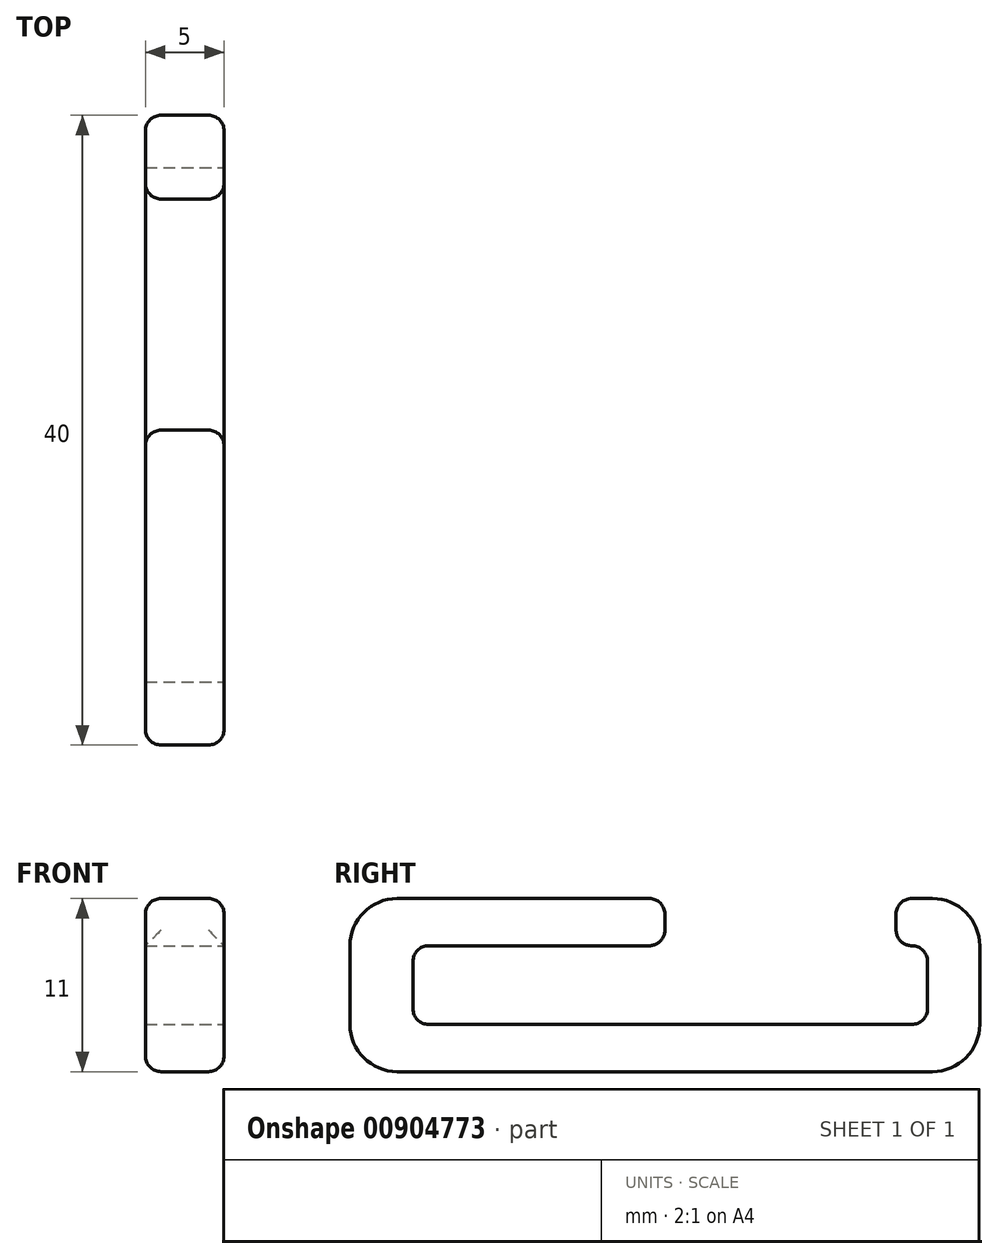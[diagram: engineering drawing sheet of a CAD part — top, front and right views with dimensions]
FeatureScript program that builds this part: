
annotation { "Feature Type Name" : "Feature", "Feature Type Description" : "" }
export const myFeature = defineFeature(function(context is Context, id is Id, definition is map)
    precondition{}
    {
        {
            var Q0;
            Q0=qCreatedBy(makeId("Top.planeOp"),FACE);
            var sketch = newSketch(context, id + "F0", { "sketchPlane" : qUnion([Q0])});
            skCircle(sketch, "E0", {"center": v(0, 0) * mm, "radius": 3 * mm, "construction": true});
            skLineSegment(sketch, "E1", {"start": v(-2.5, 1.66) * mm, "end": v(-2.5, -38.34) * mm});
            skLineSegment(sketch, "E2", {"start": v(-2.5, -38.34) * mm, "end": v(0, -38.34) * mm});
            skLineSegment(sketch, "E3.MirrorCS", {"start": v(2.5, 1.66) * mm, "end": v(2.5, -38.34) * mm});
            skLineSegment(sketch, "E4.MirrorCS", {"start": v(2.5, -38.34) * mm, "end": v(0, -38.34) * mm});
            skLineSegment(sketch, "E5", {"start": v(-2.5, -34.34) * mm, "end": v(2.5, -34.34) * mm});
            skLineSegment(sketch, "E6", {"start": v(-2.5, -18.34) * mm, "end": v(2.5, -18.34) * mm});
            skCircle(sketch, "E7", {"center": v(-5.3, 0) * mm, "radius": 12.5 * mm, "construction": true});
            skLineSegment(sketch, "E8", {"start": v(-2.5, 1.66) * mm, "end": v(2.5, 1.66) * mm});
            skLineSegment(sketch, "E9", {"start": v(-2.5, -1.66) * mm, "end": v(2.5, -1.66) * mm});
            skLineSegment(sketch, "E10", {"start": v(-2.5, -3.66) * mm, "end": v(2.5, -3.66) * mm});
            skSolve(sketch);
        }
        {
            var Q0;
            {var subQ0=sQuery(id+"F0.wireOp",EDGE,"E8");Q0=makeQuery(id+"F0.imprint","IMPRINT",FACE,{"disambiguationData":[TD([[makeQuery(id+"F0.imprint","IMPRINT",EDGE,{"derivedFrom":subQ0}),-1.0]])]});}
            var Q1;
            {var subQ0=sQuery(id+"F0.wireOp",EDGE,"E5");Q1=makeQuery(id+"F0.imprint","IMPRINT",FACE,{"disambiguationData":[TD([[makeQuery(id+"F0.imprint","IMPRINT",EDGE,{"derivedFrom":subQ0}),1.0]])]});}
            var Q2;
            {var subQ0=sQuery(id+"F0.wireOp",EDGE,"E6");Q2=makeQuery(id+"F0.imprint","IMPRINT",FACE,{"disambiguationData":[TD([[makeQuery(id+"F0.imprint","IMPRINT",EDGE,{"derivedFrom":subQ0}),1.0]])]});}
            var Q3;
            {var subQ0=sQuery(id+"F0.wireOp",EDGE,"E9");Q3=makeQuery(id+"F0.imprint","IMPRINT",FACE,{"disambiguationData":[TD([[makeQuery(id+"F0.imprint","IMPRINT",EDGE,{"derivedFrom":subQ0}),-1.0]])]});}
            var Q4;
            {var subQ3=sQuery(id+"F0.wireOp",EDGE,"E2");Q4=makeQuery(id+"F0.imprint","IMPRINT",FACE,{"disambiguationData":[TD([[makeQuery(id+"F0.imprint","IMPRINT",EDGE,{"derivedFrom":subQ3}),1.0]])]});}
            extrude(context, id + "F1", {"entities" : qUnion([Q0, Q1, Q2, Q3, Q4]), "depth" : 3 * mm, "offsetDistance" : 25 * mm});
        }
        {
            var Q0;
            {var subQ0=sQuery(id+"F0.wireOp",EDGE,"E8");Q0=makeQuery(id+"F0.imprint","IMPRINT",FACE,{"disambiguationData":[TD([[makeQuery(id+"F0.imprint","IMPRINT",EDGE,{"derivedFrom":subQ0}),-1.0]])]});}
            var Q1;
            {var subQ0=sQuery(id+"F0.wireOp",EDGE,"E9");Q1=makeQuery(id+"F0.imprint","IMPRINT",FACE,{"disambiguationData":[TD([[makeQuery(id+"F0.imprint","IMPRINT",EDGE,{"derivedFrom":subQ0}),-1.0]])]});}
            var Q2;
            {var subQ3=sQuery(id+"F0.wireOp",EDGE,"E2");Q2=makeQuery(id+"F0.imprint","IMPRINT",FACE,{"disambiguationData":[TD([[makeQuery(id+"F0.imprint","IMPRINT",EDGE,{"derivedFrom":subQ3}),1.0]])]});}
            var Q3;
            {var subQ0=sQuery(id+"F0.wireOp",EDGE,"E5");Q3=makeQuery(id+"F0.imprint","IMPRINT",FACE,{"disambiguationData":[TD([[makeQuery(id+"F0.imprint","IMPRINT",EDGE,{"derivedFrom":subQ0}),1.0]])]});}
            extrude(context, id + "F2", {"entities" : qUnion([Q0, Q1, Q2, Q3]), "operationType" : NewBodyOperationType.ADD, "depth" : 11 * mm, "offsetDistance" : 25 * mm});
        }
        {
            var Q0;
            {var subQ0=sQuery(id+"F0.wireOp",EDGE,"E9");Q0=makeQuery(id+"F0.imprint","IMPRINT",FACE,{"disambiguationData":[TD([[makeQuery(id+"F0.imprint","IMPRINT",EDGE,{"derivedFrom":subQ0}),-1.0]])]});}
            var Q1;
            {var subQ0=sQuery(id+"F0.wireOp",EDGE,"E5");Q1=makeQuery(id+"F0.imprint","IMPRINT",FACE,{"disambiguationData":[TD([[makeQuery(id+"F0.imprint","IMPRINT",EDGE,{"derivedFrom":subQ0}),1.0]])]});}
            extrude(context, id + "F3", {"entities" : qUnion([Q0, Q1]), "operationType" : NewBodyOperationType.REMOVE, "depth" : 8 * mm, "offsetDistance" : 25 * mm, "hasSecondDirection" : true, "secondDirectionOppositeDirection" : false, "secondDirectionDepth" : 3 * mm});
        }
        {
            var Q0;
            Q0=makeQuery(id+"F2.opExtrude","CAP_EDGE",EDGE,{"disambiguationData":[OSD([sQuery(id+"F0.wireOp",EDGE,"E8")])],"isStart":false});
            var Q1;
            Q1=makeQuery(id+"F2.opExtrude","CAP_EDGE",EDGE,{"disambiguationData":[OSD([sQuery(id+"F0.wireOp",EDGE,"E2"),sQuery(id+"F0.wireOp",EDGE,"E4.MirrorCS")])],"isStart":false});
            var Q2;
            Q2=makeQuery(id+"F1.opExtrude","CAP_EDGE",EDGE,{"disambiguationData":[OSD([sQuery(id+"F0.wireOp",EDGE,"E2"),sQuery(id+"F0.wireOp",EDGE,"E4.MirrorCS")])],"isStart":true});
            var Q3;
            Q3=makeQuery(id+"F1.opExtrude","CAP_EDGE",EDGE,{"disambiguationData":[OSD([sQuery(id+"F0.wireOp",EDGE,"E8")])],"isStart":true});
            fillet(context, id + "F4", {"entities" : qUnion([Q0, Q1, Q2, Q3]), "radius" : 3 * mm, "tangentPropagation" : true, "allowEdgeOverflow" : false});
        }
        {
            var Q0;
            Q0=makeQuery(id+"F3.boolean.opBoolean","COPY",EDGE,{"derivedFrom":makeQuery(id+"F3.opExtrude","CAP_EDGE",EDGE,{"disambiguationData":[OSD([sQuery(id+"F0.wireOp",EDGE,"E5")])],"isStart":false})});
            var Q1;
            Q1=makeQuery(id+"F3.boolean.opBoolean","COPY",EDGE,{"derivedFrom":makeQuery(id+"F3.opExtrude","CAP_EDGE",EDGE,{"disambiguationData":[OSD([sQuery(id+"F0.wireOp",EDGE,"E5")])],"isStart":true})});
            var Q2;
            Q2=makeQuery(id+"F3.boolean.opBoolean","COPY",EDGE,{"derivedFrom":makeQuery(id+"F3.opExtrude","CAP_EDGE",EDGE,{"disambiguationData":[OSD([sQuery(id+"F0.wireOp",EDGE,"E9")])],"isStart":true})});
            var Q3;
            Q3=makeQuery(id+"F3.boolean.opBoolean","COPY",EDGE,{"derivedFrom":makeQuery(id+"F3.opExtrude","CAP_EDGE",EDGE,{"disambiguationData":[OSD([sQuery(id+"F0.wireOp",EDGE,"E9")])],"isStart":false})});
            var Q4;
            {var subQ0=sQuery(id+"F0.wireOp",EDGE,"E1");var subQ1=makeQuery(id+"F0.imprint","INTERSECT",VERTEX,{"derivedFrom":[subQ0,sQuery(id+"F0.wireOp",EDGE,"E5")]});Q4=makeQuery(id+"F2.opExtrude","CAP_EDGE",EDGE,{"disambiguationData":[OSD([subQ0]),TDD([makeQuery(id+"F0.imprint","IMPRINT",EDGE,{"disambiguationData":[TD([[subQ1,1.0]])],"derivedFrom":subQ0}),makeQuery(id+"F0.imprint","IMPRINT",EDGE,{"disambiguationData":[TD([[makeQuery(id+"F0.imprint","INTERSECT",VERTEX,{"derivedFrom":[subQ0,sQuery(id+"F0.wireOp",EDGE,"E2")]}),1.0]])],"derivedFrom":subQ0})])],"isStart":false});}
            var Q5;
            {var subQ0=sQuery(id+"F0.wireOp",EDGE,"E3.MirrorCS");var subQ1=makeQuery(id+"F0.imprint","INTERSECT",VERTEX,{"derivedFrom":[subQ0,sQuery(id+"F0.wireOp",EDGE,"E5")]});Q5=makeQuery(id+"F2.opExtrude","CAP_EDGE",EDGE,{"disambiguationData":[OSD([subQ0]),TDD([makeQuery(id+"F0.imprint","IMPRINT",EDGE,{"disambiguationData":[TD([[subQ1,1.0]])],"derivedFrom":subQ0}),makeQuery(id+"F0.imprint","IMPRINT",EDGE,{"disambiguationData":[TD([[makeQuery(id+"F0.imprint","INTERSECT",VERTEX,{"derivedFrom":[subQ0,sQuery(id+"F0.wireOp",EDGE,"E4.MirrorCS")]}),1.0]])],"derivedFrom":subQ0})])],"isStart":false});}
            var Q6;
            Q6=makeQuery(id+"F2.opExtrude","SWEPT_FACE",FACE,{"disambiguationData":[OSD([sQuery(id+"F0.wireOp",EDGE,"E10")])]});
            var Q7;
            Q7=makeQuery(id+"F2.opExtrude","SWEPT_FACE",FACE,{"disambiguationData":[OSD([sQuery(id+"F0.wireOp",EDGE,"E6")])]});
            var Q8;
            {var subQ0=sQuery(id+"F0.wireOp",EDGE,"E3.MirrorCS");Q8=makeQuery(id+"F3.boolean.opBoolean","MERGE",EDGE,{"derivedFrom":[makeQuery(id+"F1.opExtrude","CAP_EDGE",EDGE,{"disambiguationData":[OSD([subQ0])],"isStart":false})],"fromTools":[makeQuery(id+"F3.opExtrude","CAP_EDGE",EDGE,{"disambiguationData":[OSD([subQ0]),TDD([makeQuery(id+"F0.imprint","IMPRINT",EDGE,{"disambiguationData":[TD([[makeQuery(id+"F0.imprint","INTERSECT",VERTEX,{"derivedFrom":[subQ0,sQuery(id+"F0.wireOp",EDGE,"E9")]}),-1.0]])],"derivedFrom":subQ0})])],"isStart":true}),makeQuery(id+"F3.opExtrude","CAP_EDGE",EDGE,{"disambiguationData":[OSD([subQ0]),TDD([makeQuery(id+"F0.imprint","IMPRINT",EDGE,{"disambiguationData":[TD([[makeQuery(id+"F0.imprint","INTERSECT",VERTEX,{"derivedFrom":[subQ0,sQuery(id+"F0.wireOp",EDGE,"E5")]}),1.0]])],"derivedFrom":subQ0})])],"isStart":true})]});}
            var Q9;
            {var subQ0=sQuery(id+"F0.wireOp",EDGE,"E1");Q9=makeQuery(id+"F3.boolean.opBoolean","MERGE",EDGE,{"derivedFrom":[makeQuery(id+"F1.opExtrude","CAP_EDGE",EDGE,{"disambiguationData":[OSD([subQ0])],"isStart":false})],"fromTools":[makeQuery(id+"F3.opExtrude","CAP_EDGE",EDGE,{"disambiguationData":[OSD([subQ0]),TDD([makeQuery(id+"F0.imprint","IMPRINT",EDGE,{"disambiguationData":[TD([[makeQuery(id+"F0.imprint","INTERSECT",VERTEX,{"derivedFrom":[subQ0,sQuery(id+"F0.wireOp",EDGE,"E9")]}),-1.0]])],"derivedFrom":subQ0})])],"isStart":true}),makeQuery(id+"F3.opExtrude","CAP_EDGE",EDGE,{"disambiguationData":[OSD([subQ0]),TDD([makeQuery(id+"F0.imprint","IMPRINT",EDGE,{"disambiguationData":[TD([[makeQuery(id+"F0.imprint","INTERSECT",VERTEX,{"derivedFrom":[subQ0,sQuery(id+"F0.wireOp",EDGE,"E5")]}),1.0]])],"derivedFrom":subQ0})])],"isStart":true})]});}
            fillet(context, id + "F5", {"entities" : qUnion([Q0, Q1, Q2, Q3, Q4, Q5, Q6, Q7, Q8, Q9]), "radius" : 1 * mm, "tangentPropagation" : true, "allowEdgeOverflow" : false});
        }
    });
